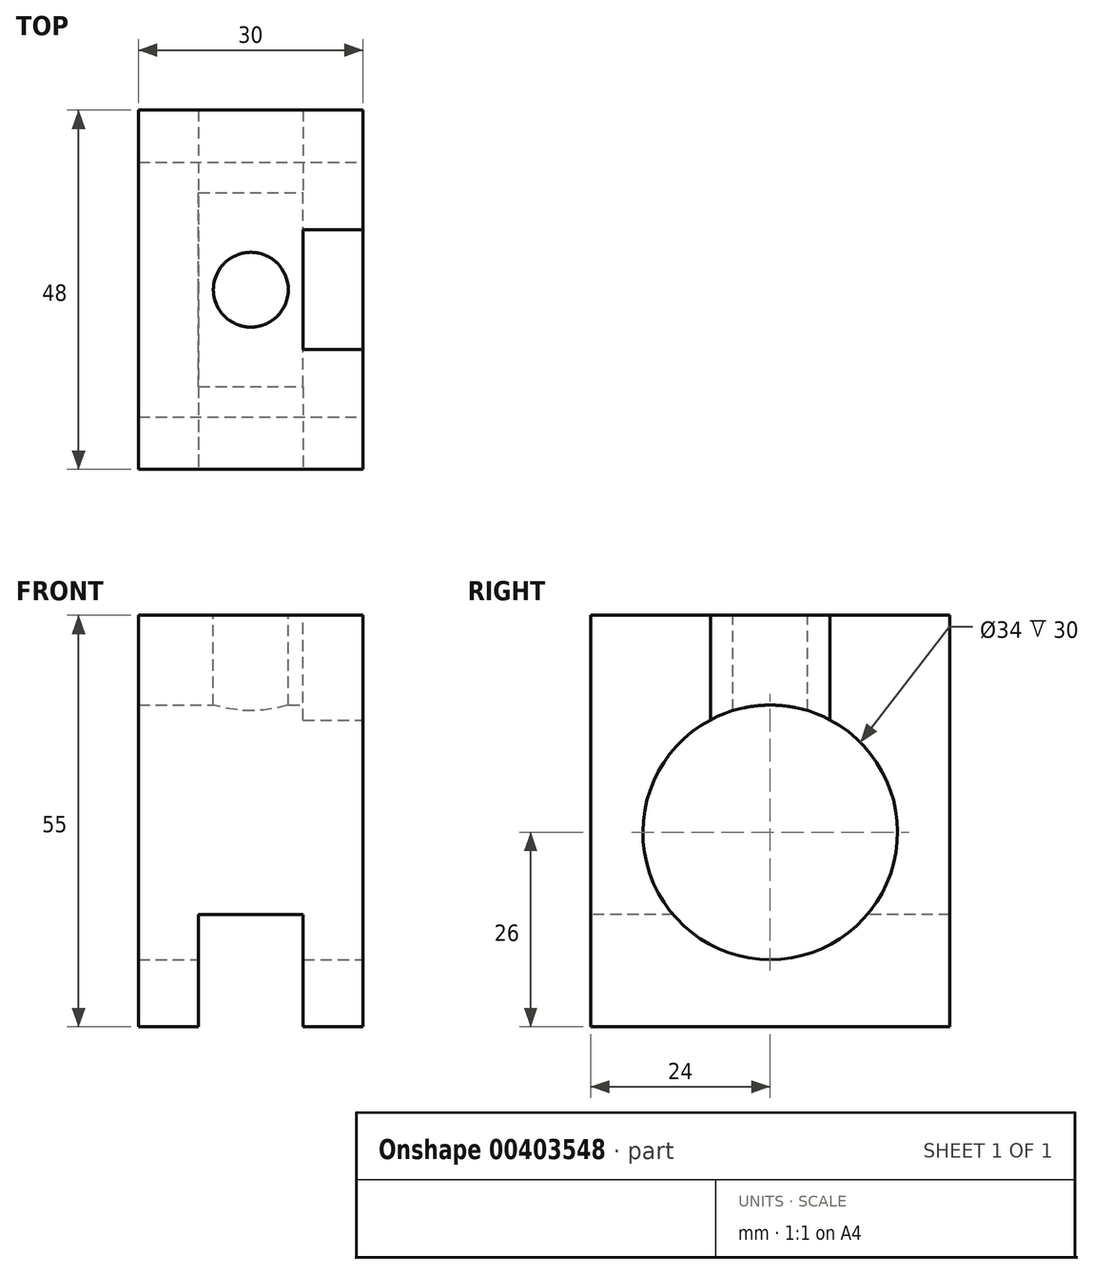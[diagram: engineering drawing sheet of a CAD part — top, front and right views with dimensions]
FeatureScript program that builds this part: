
annotation { "Feature Type Name" : "Feature", "Feature Type Description" : "" }
export const myFeature = defineFeature(function(context is Context, id is Id, definition is map)
    precondition{}
    {
        {
            var Q0;
            Q0=qCreatedBy(makeId("Right.planeOp"),FACE);
            var sketch = newSketch(context, id + "F0", { "sketchPlane" : qUnion([Q0])});
            skLineSegment(sketch, "E0.bottom", {"start": v(-24, 27.5) * mm, "end": v(24, 27.5) * mm});
            skLineSegment(sketch, "E0.top", {"start": v(-24, -27.5) * mm, "end": v(24, -27.5) * mm});
            skLineSegment(sketch, "E0.left", {"start": v(-24, 27.5) * mm, "end": v(-24, -27.5) * mm});
            skLineSegment(sketch, "E0.right", {"start": v(24, 27.5) * mm, "end": v(24, -27.5) * mm});
            skPoint(sketch, "E0.middle", {"position": v(0, 0) * mm});
            skSolve(sketch);
        }
        {
            var Q0;
            Q0 = qSketchRegion(id + "F0", true);
            extrude(context, id + "F1", {"entities" : qUnion([Q0]), "endBound" : BoundingType.SYMMETRIC, "depth" : 30 * mm});
        }
        {
            var Q0;
            Q0=makeQuery(id+"F1.opExtrude","CAP_FACE",FACE,{"disambiguationData":[OSD([sQuery(id+"F0.wireOp",EDGE,"E0.bottom"),sQuery(id+"F0.wireOp",EDGE,"E0.top"),sQuery(id+"F0.wireOp",EDGE,"E0.left"),sQuery(id+"F0.wireOp",EDGE,"E0.right")])],"isStart":false});
            var sketch = newSketch(context, id + "F2", { "sketchPlane" : qUnion([Q0])});
            skCircle(sketch, "E1", {"center": v(0, -1.5) * mm, "radius": 17 * mm});
            skSolve(sketch);
        }
        {
            var Q0;
            Q0 = qSketchRegion(id + "F2", true);
            extrude(context, id + "F3", {"entities" : qUnion([Q0]), "operationType" : NewBodyOperationType.REMOVE, "endBound" : BoundingType.THROUGH_ALL, "oppositeDirection" : true, "depth" : 25 * mm});
        }
        {
            var Q0;
            Q0=makeQuery(id+"F1.opExtrude","SWEPT_FACE",FACE,{"disambiguationData":[OSD([sQuery(id+"F0.wireOp",EDGE,"E0.bottom")])]});
            var sketch = newSketch(context, id + "F4", { "sketchPlane" : qUnion([Q0])});
            skLineSegment(sketch, "E2.bottom", {"start": v(7, -8) * mm, "end": v(15, -8) * mm});
            skLineSegment(sketch, "E2.top", {"start": v(7, 8) * mm, "end": v(15, 8) * mm});
            skLineSegment(sketch, "E2.left", {"start": v(7, -8) * mm, "end": v(7, 8) * mm});
            skLineSegment(sketch, "E2.right", {"start": v(15, -8) * mm, "end": v(15, 8) * mm});
            skSolve(sketch);
        }
        {
            var Q0;
            Q0 = qSketchRegion(id + "F4", true);
            var Q1;
            Q1=makeQuery(id+"F3.boolean.opBoolean","COPY",FACE,{"derivedFrom":makeQuery(id+"F3.opExtrude","SWEPT_FACE",FACE,{"disambiguationData":[OSD([sQuery(id+"F2.wireOp",EDGE,"E1")])]})});
            extrude(context, id + "F5", {"entities" : qUnion([Q0]), "operationType" : NewBodyOperationType.REMOVE, "endBound" : BoundingType.UP_TO_SURFACE, "oppositeDirection" : true, "endBoundEntityFace" : qUnion([Q1]), "depth" : 25 * mm});
        }
        {
            var Q0;
            Q0=makeQuery(id+"F1.opExtrude","SWEPT_FACE",FACE,{"disambiguationData":[OSD([sQuery(id+"F0.wireOp",EDGE,"E0.bottom")])]});
            var sketch = newSketch(context, id + "F6", { "sketchPlane" : qUnion([Q0])});
            skCircle(sketch, "E3", {"center": v(0, 0) * mm, "radius": 5 * mm});
            skSolve(sketch);
        }
        {
            var Q0;
            Q0 = qSketchRegion(id + "F6", true);
            var Q1;
            Q1=makeQuery(id+"F3.boolean.opBoolean","COPY",FACE,{"derivedFrom":makeQuery(id+"F3.opExtrude","SWEPT_FACE",FACE,{"disambiguationData":[OSD([sQuery(id+"F2.wireOp",EDGE,"E1")])]})});
            extrude(context, id + "F7", {"entities" : qUnion([Q0]), "operationType" : NewBodyOperationType.REMOVE, "endBound" : BoundingType.UP_TO_SURFACE, "oppositeDirection" : true, "endBoundEntityFace" : qUnion([Q1]), "depth" : 25 * mm});
        }
        {
            var Q0;
            Q0=makeQuery(id+"F1.opExtrude","SWEPT_FACE",FACE,{"disambiguationData":[OSD([sQuery(id+"F0.wireOp",EDGE,"E0.left")])]});
            var sketch = newSketch(context, id + "F8", { "sketchPlane" : qUnion([Q0])});
            skLineSegment(sketch, "E4.bottom", {"start": v(-7, -27.5) * mm, "end": v(7, -27.5) * mm});
            skLineSegment(sketch, "E4.top", {"start": v(-7, -12.5) * mm, "end": v(7, -12.5) * mm});
            skLineSegment(sketch, "E4.left", {"start": v(-7, -27.5) * mm, "end": v(-7, -12.5) * mm});
            skLineSegment(sketch, "E4.right", {"start": v(7, -27.5) * mm, "end": v(7, -12.5) * mm});
            skSolve(sketch);
        }
        {
            var Q0;
            Q0 = qSketchRegion(id + "F8", true);
            extrude(context, id + "F9", {"entities" : qUnion([Q0]), "operationType" : NewBodyOperationType.REMOVE, "endBound" : BoundingType.THROUGH_ALL, "oppositeDirection" : true, "depth" : 25 * mm});
        }
    });
